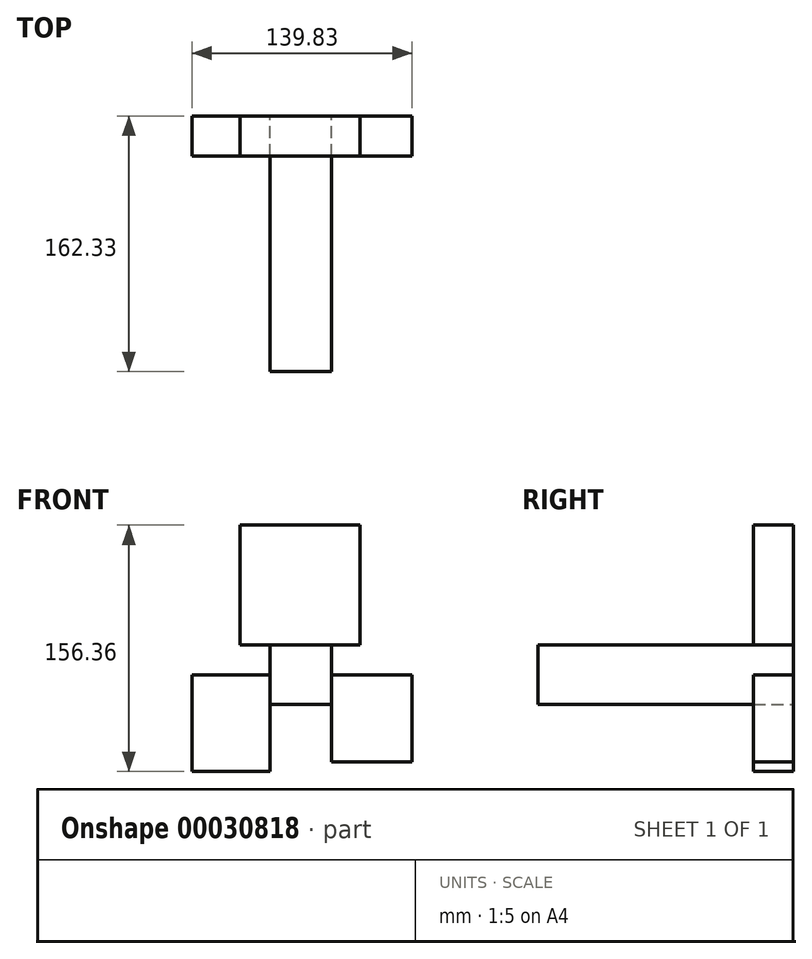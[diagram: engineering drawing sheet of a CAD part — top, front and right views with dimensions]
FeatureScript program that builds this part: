
annotation { "Feature Type Name" : "Feature", "Feature Type Description" : "" }
export const myFeature = defineFeature(function(context is Context, id is Id, definition is map)
    precondition{}
    {
        {
            var Q0;
            Q0=qCreatedBy(makeId("Front.planeOp"),FACE);
            var sketch = newSketch(context, id + "F0", { "sketchPlane" : qUnion([Q0])});
            skLineSegment(sketch, "E0", {"start": v(0, 0) * mm, "end": v(38.1, 0) * mm});
            skLineSegment(sketch, "E1", {"start": v(38.1, 0) * mm, "end": v(38.1, 76.2) * mm});
            skLineSegment(sketch, "E2", {"start": v(38.1, 76.2) * mm, "end": v(0, 76.2) * mm});
            skLineSegment(sketch, "E3", {"start": v(0, 76.2) * mm, "end": v(0, 0) * mm});
            skLineSegment(sketch, "E4.bottom", {"start": v(0, 0) * mm, "end": v(-38.1, 0) * mm});
            skLineSegment(sketch, "E4.top", {"start": v(0, 76.2) * mm, "end": v(-38.1, 76.2) * mm});
            skLineSegment(sketch, "E4.left", {"start": v(0, 0) * mm, "end": v(0, 76.2) * mm});
            skLineSegment(sketch, "E4.right", {"start": v(-38.1, 0) * mm, "end": v(-38.1, 76.2) * mm});
            skLineSegment(sketch, "E5.bottom", {"start": v(-19.05, 0) * mm, "end": v(20.17, 0) * mm});
            skLineSegment(sketch, "E5.top", {"start": v(-19.05, -37.5) * mm, "end": v(20.17, -37.5) * mm});
            skLineSegment(sketch, "E5.left", {"start": v(-19.05, 0) * mm, "end": v(-19.05, -37.5) * mm});
            skLineSegment(sketch, "E5.right", {"start": v(20.17, 0) * mm, "end": v(20.17, -37.5) * mm});
            skLineSegment(sketch, "E6.bottom", {"start": v(-19.05, -18.75) * mm, "end": v(-68.56, -18.75) * mm});
            skLineSegment(sketch, "E6.top", {"start": v(-19.05, -80.16) * mm, "end": v(-68.56, -80.16) * mm});
            skLineSegment(sketch, "E6.left", {"start": v(-19.05, -18.75) * mm, "end": v(-19.05, -80.16) * mm});
            skLineSegment(sketch, "E6.right", {"start": v(-68.56, -18.75) * mm, "end": v(-68.56, -80.16) * mm});
            skLineSegment(sketch, "E7.bottom", {"start": v(20.17, -18.75) * mm, "end": v(71.27, -18.75) * mm});
            skLineSegment(sketch, "E7.top", {"start": v(20.17, -74.27) * mm, "end": v(71.27, -74.27) * mm});
            skLineSegment(sketch, "E7.left", {"start": v(20.17, -18.75) * mm, "end": v(20.17, -74.27) * mm});
            skLineSegment(sketch, "E7.right", {"start": v(71.27, -18.75) * mm, "end": v(71.27, -74.27) * mm});
            skSolve(sketch);
        }
        {
            var Q0;
            {var subQ2=sQuery(id+"F0.wireOp",EDGE,"E4.bottom");Q0=makeQuery(id+"F0.imprint","IMPRINT",FACE,{"disambiguationData":[TD([[makeQuery(id+"F0.imprint","IMPRINT",EDGE,{"derivedFrom":subQ2}),-1.0]])]});}
            var Q1;
            {var subQ2=sQuery(id+"F0.wireOp",EDGE,"E0");Q1=makeQuery(id+"F0.imprint","IMPRINT",FACE,{"disambiguationData":[TD([[makeQuery(id+"F0.imprint","IMPRINT",EDGE,{"derivedFrom":subQ2}),1.0]])]});}
            var Q2;
            {var subQ3=sQuery(id+"F0.wireOp",EDGE,"E6.bottom");Q2=makeQuery(id+"F0.imprint","IMPRINT",FACE,{"disambiguationData":[TD([[makeQuery(id+"F0.imprint","IMPRINT",EDGE,{"derivedFrom":subQ3}),1.0]])]});}
            var Q3;
            {var subQ3=sQuery(id+"F0.wireOp",EDGE,"E7.bottom");Q3=makeQuery(id+"F0.imprint","IMPRINT",FACE,{"disambiguationData":[TD([[makeQuery(id+"F0.imprint","IMPRINT",EDGE,{"derivedFrom":subQ3}),-1.0]])]});}
            extrude(context, id + "F1", {"entities" : qUnion([Q0, Q1, Q2, Q3]), "depth" : 25.4 * mm});
        }
        {
            var Q0;
            {var subQ2=sQuery(id+"F0.wireOp",EDGE,"E5.top");Q0=makeQuery(id+"F0.imprint","IMPRINT",FACE,{"disambiguationData":[TD([[makeQuery(id+"F0.imprint","IMPRINT",EDGE,{"derivedFrom":subQ2}),1.0]])]});}
            extrude(context, id + "F2", {"entities" : qUnion([Q0]), "depth" : 162.33 * mm});
        }
    });
